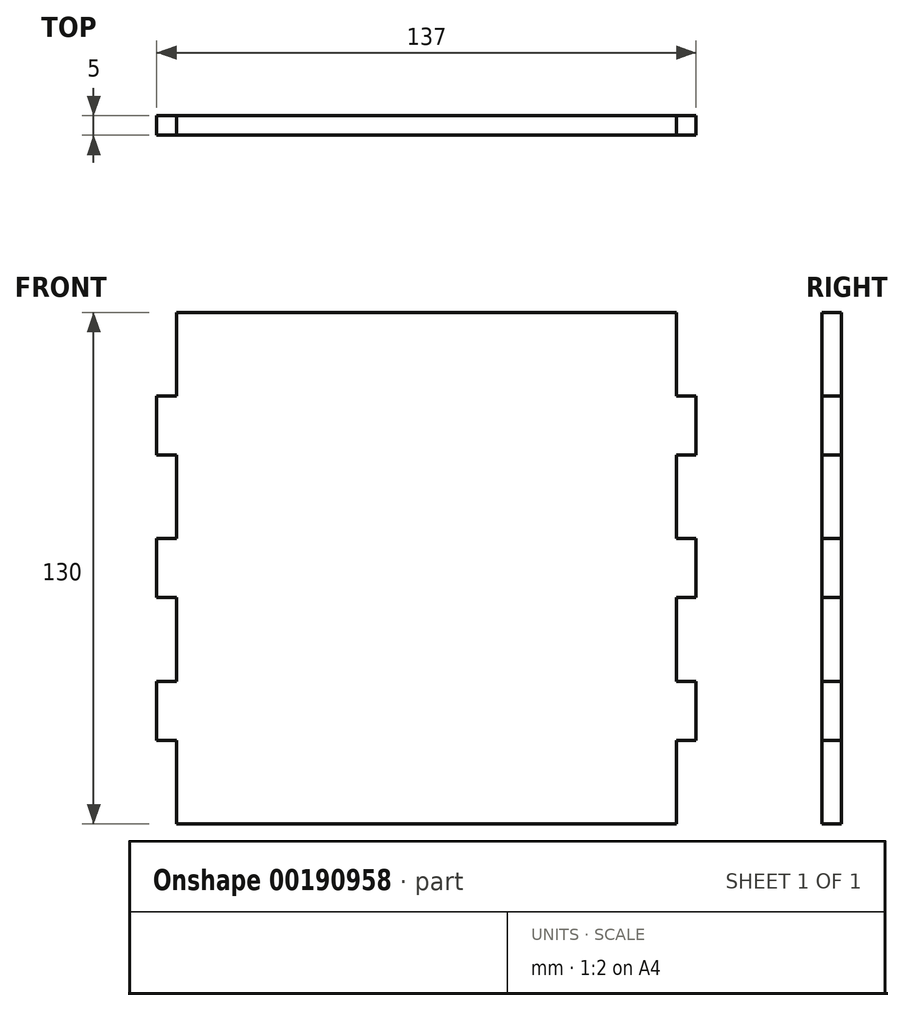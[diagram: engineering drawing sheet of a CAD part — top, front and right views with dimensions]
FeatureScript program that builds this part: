
annotation { "Feature Type Name" : "Feature", "Feature Type Description" : "" }
export const myFeature = defineFeature(function(context is Context, id is Id, definition is map)
    precondition{}
    {
        {
            var Q0;
            Q0=qCreatedBy(makeId("Front.planeOp"),FACE);
            var sketch = newSketch(context, id + "F0", { "sketchPlane" : qUnion([Q0])});
            skLineSegment(sketch, "E0.bottom", {"start": v(0, 0) * mm, "end": v(127, 0) * mm});
            skLineSegment(sketch, "E0.top", {"start": v(0, 130) * mm, "end": v(127, 130) * mm});
            skLineSegment(sketch, "E0.left", {"start": v(0, 0) * mm, "end": v(0, 130) * mm});
            skLineSegment(sketch, "E0.right", {"start": v(127, 0) * mm, "end": v(127, 130) * mm});
            skLineSegment(sketch, "E1.bottom", {"start": v(127, 108.75) * mm, "end": v(132, 108.75) * mm});
            skLineSegment(sketch, "E1.top", {"start": v(127, 93.75) * mm, "end": v(132, 93.75) * mm});
            skLineSegment(sketch, "E1.left", {"start": v(127, 108.75) * mm, "end": v(127, 93.75) * mm});
            skLineSegment(sketch, "E1.right", {"start": v(132, 108.75) * mm, "end": v(132, 93.75) * mm});
            skLineSegment(sketch, "E2.bottom", {"start": v(127, 57.5) * mm, "end": v(132, 57.5) * mm});
            skLineSegment(sketch, "E2.top", {"start": v(127, 72.5) * mm, "end": v(132, 72.5) * mm});
            skLineSegment(sketch, "E2.left", {"start": v(127, 57.5) * mm, "end": v(127, 72.5) * mm});
            skLineSegment(sketch, "E2.right", {"start": v(132, 57.5) * mm, "end": v(132, 72.5) * mm});
            skLineSegment(sketch, "E3.bottom", {"start": v(127, 21.25) * mm, "end": v(132, 21.25) * mm});
            skLineSegment(sketch, "E3.top", {"start": v(127, 36.25) * mm, "end": v(132, 36.25) * mm});
            skLineSegment(sketch, "E3.left", {"start": v(127, 21.25) * mm, "end": v(127, 36.25) * mm});
            skLineSegment(sketch, "E3.right", {"start": v(132, 21.25) * mm, "end": v(132, 36.25) * mm});
            skLineSegment(sketch, "E4.bottom", {"start": v(0, 21.25) * mm, "end": v(-5, 21.25) * mm});
            skLineSegment(sketch, "E4.top", {"start": v(0, 36.25) * mm, "end": v(-5, 36.25) * mm});
            skLineSegment(sketch, "E4.left", {"start": v(0, 21.25) * mm, "end": v(0, 36.25) * mm});
            skLineSegment(sketch, "E4.right", {"start": v(-5, 21.25) * mm, "end": v(-5, 36.25) * mm});
            skLineSegment(sketch, "E5.bottom", {"start": v(-5, 57.5) * mm, "end": v(0, 57.5) * mm});
            skLineSegment(sketch, "E5.top", {"start": v(-5, 72.5) * mm, "end": v(0, 72.5) * mm});
            skLineSegment(sketch, "E5.left", {"start": v(-5, 57.5) * mm, "end": v(-5, 72.5) * mm});
            skLineSegment(sketch, "E5.right", {"start": v(0, 57.5) * mm, "end": v(0, 72.5) * mm});
            skLineSegment(sketch, "E6.bottom", {"start": v(-5, 93.75) * mm, "end": v(0, 93.75) * mm});
            skLineSegment(sketch, "E6.top", {"start": v(-5, 108.75) * mm, "end": v(0, 108.75) * mm});
            skLineSegment(sketch, "E6.left", {"start": v(-5, 93.75) * mm, "end": v(-5, 108.75) * mm});
            skLineSegment(sketch, "E6.right", {"start": v(0, 93.75) * mm, "end": v(0, 108.75) * mm});
            skSolve(sketch);
        }
        {
            var Q0;
            Q0 = qSketchRegion(id + "F0", true);
            extrude(context, id + "F1", {"entities" : qUnion([Q0]), "depth" : 5 * mm});
        }
    });
